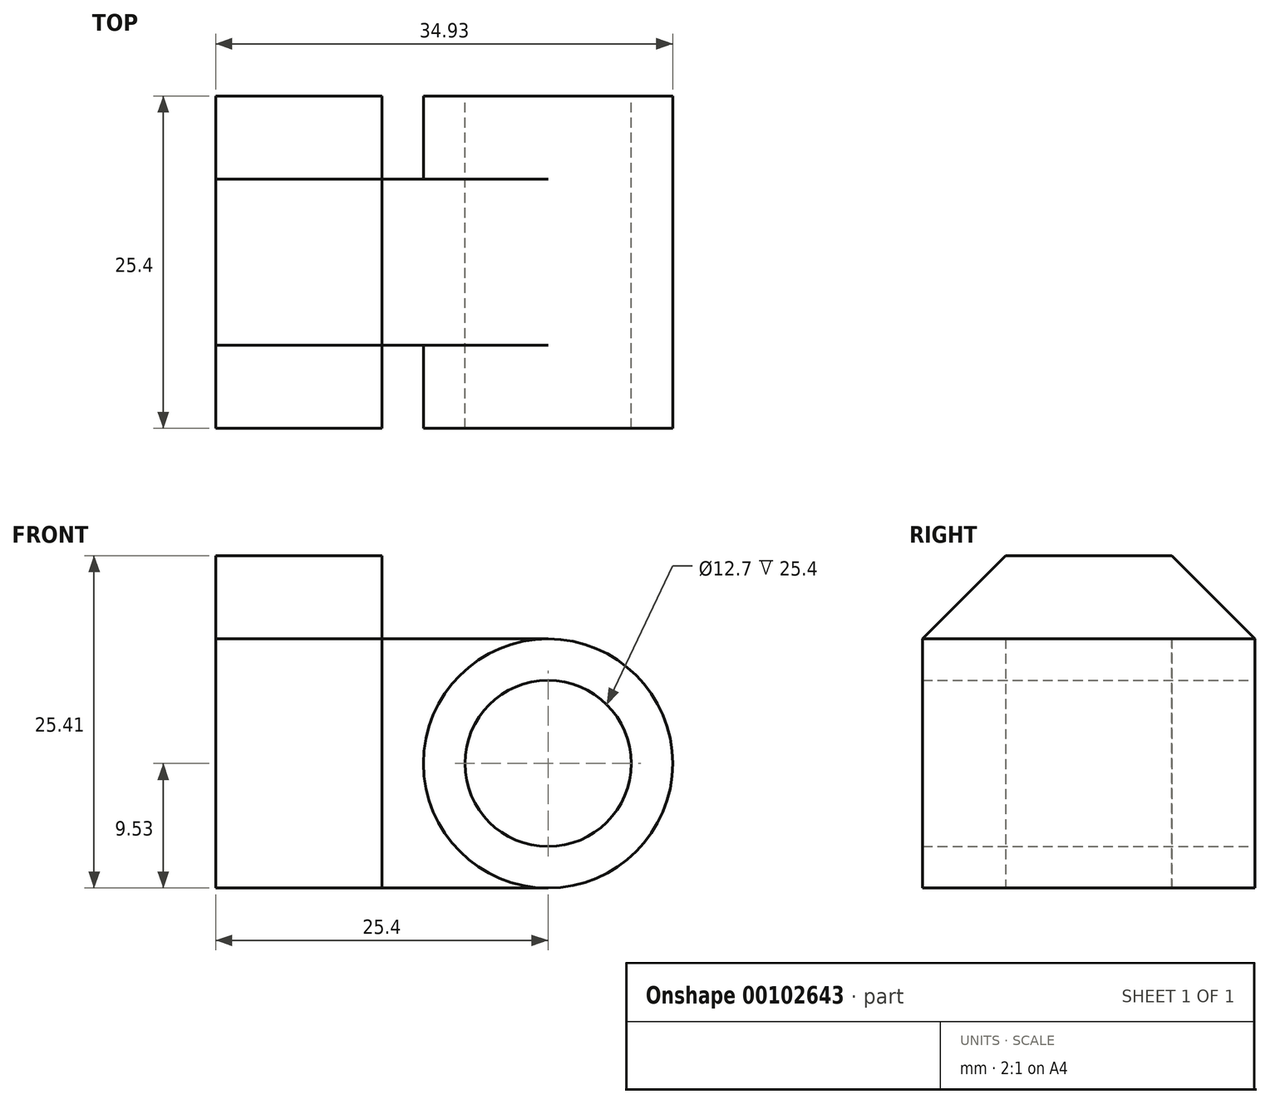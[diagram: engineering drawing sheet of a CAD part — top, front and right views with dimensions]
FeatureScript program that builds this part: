
annotation { "Feature Type Name" : "Feature", "Feature Type Description" : "" }
export const myFeature = defineFeature(function(context is Context, id is Id, definition is map)
    precondition{}
    {
        {
            var Q0;
            Q0=qCreatedBy(makeId("Front.planeOp"),FACE);
            var sketch = newSketch(context, id + "F0", { "sketchPlane" : qUnion([Q0])});
            skCircle(sketch, "E0", {"center": v(0, 0) * mm, "radius": 9.53 * mm});
            skCircle(sketch, "E1", {"center": v(0, 0) * mm, "radius": 6.35 * mm});
            skLineSegment(sketch, "E2", {"start": v(0, -9.53) * mm, "end": v(-12.7, -9.53) * mm});
            skLineSegment(sketch, "E3", {"start": v(0, 9.53) * mm, "end": v(-12.7, 9.53) * mm});
            skLineSegment(sketch, "E4", {"start": v(-12.7, -9.53) * mm, "end": v(-12.7, 9.52) * mm});
            skLineSegment(sketch, "E5", {"start": v(-12.7, -9.53) * mm, "end": v(-25.4, -9.53) * mm});
            skLineSegment(sketch, "E6", {"start": v(-25.4, -9.53) * mm, "end": v(-25.4, 15.87) * mm});
            skLineSegment(sketch, "E7", {"start": v(-25.4, 15.87) * mm, "end": v(-12.7, 15.87) * mm});
            skLineSegment(sketch, "E8", {"start": v(-12.7, 15.87) * mm, "end": v(-12.7, 9.52) * mm});
            skSolve(sketch);
        }
        {
            var Q0;
            Q0 = qSketchRegion(id + "F0", true);
            extrude(context, id + "F1", {"entities" : qUnion([Q0]), "endBound" : BoundingType.SYMMETRIC, "depth" : 25.4 * mm});
        }
        {
            var Q0;
            Q0=makeQuery(id+"F1.opExtrude","CAP_FACE",FACE,{"disambiguationData":[OSD([sQuery(id+"F0.wireOp",EDGE,"E0"),sQuery(id+"F0.wireOp",EDGE,"E1"),sQuery(id+"F0.wireOp",EDGE,"E2"),sQuery(id+"F0.wireOp",EDGE,"E3"),sQuery(id+"F0.wireOp",EDGE,"E5"),sQuery(id+"F0.wireOp",EDGE,"E6"),sQuery(id+"F0.wireOp",EDGE,"E7"),sQuery(id+"F0.wireOp",EDGE,"E8")])],"isStart":false});
            var sketch = newSketch(context, id + "F2", { "sketchPlane" : qUnion([Q0])});
            skArc(sketch, "E9", {"start": v(0, 9.53) * mm, "mid": v(-9.53, 0) * mm, "end": v(0, -9.53) * mm});
            skLineSegment(sketch, "E10", {"start": v(-12.7, 9.52) * mm, "end": v(-12.7, -9.52) * mm});
            skSolve(sketch);
        }
        {
            var Q0;
            {var subQ0=sQuery(id+"F2.wireOp",EDGE,"E9");Q0=makeQuery(id+"F2.imprint","IMPRINT",FACE,{"disambiguationData":[TD([[makeQuery(id+"F2.imprint","IMPRINT",EDGE,{"derivedFrom":subQ0}),-1.0]])]});}
            extrude(context, id + "F3", {"entities" : qUnion([Q0]), "operationType" : NewBodyOperationType.REMOVE, "oppositeDirection" : true, "depth" : 6.35 * mm});
        }
        {
            var Q0;
            Q0=makeQuery(id+"F1.opExtrude","CAP_FACE",FACE,{"disambiguationData":[OSD([sQuery(id+"F0.wireOp",EDGE,"E0"),sQuery(id+"F0.wireOp",EDGE,"E1"),sQuery(id+"F0.wireOp",EDGE,"E2"),sQuery(id+"F0.wireOp",EDGE,"E3"),sQuery(id+"F0.wireOp",EDGE,"E5"),sQuery(id+"F0.wireOp",EDGE,"E6"),sQuery(id+"F0.wireOp",EDGE,"E7"),sQuery(id+"F0.wireOp",EDGE,"E8")])],"isStart":true});
            var sketch = newSketch(context, id + "F4", { "sketchPlane" : qUnion([Q0])});
            skLineSegment(sketch, "E11", {"start": v(12.7, 9.52) * mm, "end": v(12.7, -9.52) * mm});
            skArc(sketch, "E12", {"start": v(0, -9.53) * mm, "mid": v(9.52, 0) * mm, "end": v(0, 9.53) * mm});
            skSolve(sketch);
        }
        {
            var Q0;
            {var subQ0=sQuery(id+"F4.wireOp",EDGE,"E11");Q0=makeQuery(id+"F4.imprint","IMPRINT",FACE,{"disambiguationData":[TD([[makeQuery(id+"F4.imprint","IMPRINT",EDGE,{"derivedFrom":subQ0}),-1.0]])]});}
            extrude(context, id + "F5", {"entities" : qUnion([Q0]), "operationType" : NewBodyOperationType.REMOVE, "oppositeDirection" : true, "depth" : 6.35 * mm});
        }
        {
            var Q0;
            Q0=makeQuery(id+"F5.boolean.opBoolean","MERGE",FACE,{"derivedFrom":[makeQuery(id+"F3.boolean.opBoolean","MERGE",FACE,{"derivedFrom":[makeQuery(id+"F1.opExtrude","SWEPT_FACE",FACE,{"disambiguationData":[OSD([sQuery(id+"F0.wireOp",EDGE,"E8")])]}),makeQuery(id+"F3.opExtrude","SWEPT_FACE",FACE,{"disambiguationData":[OSD([sQuery(id+"F2.wireOp",EDGE,"E10")])]})]}),makeQuery(id+"F5.opExtrude","SWEPT_FACE",FACE,{"disambiguationData":[OSD([sQuery(id+"F4.wireOp",EDGE,"E11")])]})]});
            var sketch = newSketch(context, id + "F6", { "sketchPlane" : qUnion([Q0])});
            skLineSegment(sketch, "E13", {"start": v(-6.35, 15.87) * mm, "end": v(-12.7, 9.52) * mm});
            skLineSegment(sketch, "E14", {"start": v(6.35, 15.87) * mm, "end": v(12.7, 9.52) * mm});
            skSolve(sketch);
        }
        {
            var Q0;
            {var subQ0=sQuery(id+"F6.wireOp",EDGE,"E13");Q0=makeQuery(id+"F6.imprint","IMPRINT",FACE,{"disambiguationData":[TD([[makeQuery(id+"F6.imprint","IMPRINT",EDGE,{"derivedFrom":subQ0}),-1.0]])]});}
            var Q1;
            {var subQ0=sQuery(id+"F6.wireOp",EDGE,"E14");Q1=makeQuery(id+"F6.imprint","IMPRINT",FACE,{"disambiguationData":[TD([[makeQuery(id+"F6.imprint","IMPRINT",EDGE,{"derivedFrom":subQ0}),1.0]])]});}
            extrude(context, id + "F7", {"entities" : qUnion([Q0, Q1]), "operationType" : NewBodyOperationType.REMOVE, "endBound" : BoundingType.THROUGH_ALL, "oppositeDirection" : true, "depth" : 25.4 * mm});
        }
    });
